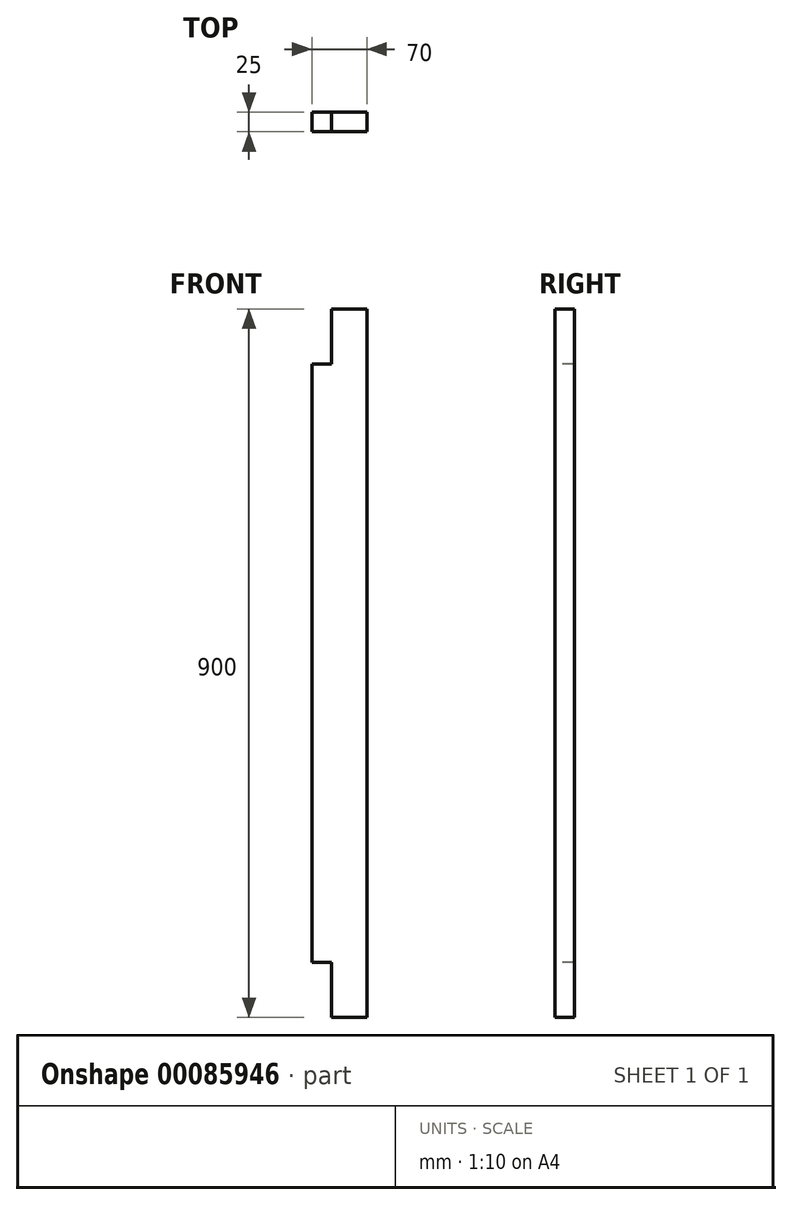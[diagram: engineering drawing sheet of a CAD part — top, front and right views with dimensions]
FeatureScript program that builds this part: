
annotation { "Feature Type Name" : "Feature", "Feature Type Description" : "" }
export const myFeature = defineFeature(function(context is Context, id is Id, definition is map)
    precondition{}
    {
        {
            var Q0;
            Q0=qCreatedBy(makeId("Front.planeOp"),FACE);
            var sketch = newSketch(context, id + "F0", { "sketchPlane" : qUnion([Q0])});
            skLineSegment(sketch, "E0.bottom", {"start": v(35, -450) * mm, "end": v(-35, -450) * mm});
            skLineSegment(sketch, "E0.top", {"start": v(35, 450) * mm, "end": v(-35, 450) * mm});
            skLineSegment(sketch, "E0.left", {"start": v(35, -450) * mm, "end": v(35, 450) * mm});
            skLineSegment(sketch, "E0.right", {"start": v(-35, -450) * mm, "end": v(-35, 450) * mm});
            skPoint(sketch, "E0.middle", {"position": v(0, 0) * mm});
            skSolve(sketch);
        }
        {
            var Q0;
            Q0=makeQuery(id+"F0.imprint","IMPRINT",FACE,{"disambiguationData":[TD([[makeQuery(id+"F0.imprint","IMPRINT",EDGE,{"derivedFrom":sQuery(id+"F0.wireOp",EDGE,"E0.bottom")}),-1.0]])]});
            extrude(context, id + "F1", {"entities" : qUnion([Q0]), "depth" : 25 * mm});
        }
        {
            var Q0;
            Q0=makeQuery(id+"F1.opExtrude","CAP_FACE",FACE,{"disambiguationData":[OSD([sQuery(id+"F0.wireOp",EDGE,"E0.bottom"),sQuery(id+"F0.wireOp",EDGE,"E0.top"),sQuery(id+"F0.wireOp",EDGE,"E0.left"),sQuery(id+"F0.wireOp",EDGE,"E0.right")])],"isStart":false});
            var sketch = newSketch(context, id + "F2", { "sketchPlane" : qUnion([Q0])});
            skLineSegment(sketch, "E1.bottom", {"start": v(-35, 450) * mm, "end": v(-10, 450) * mm});
            skLineSegment(sketch, "E1.top", {"start": v(-35, 380) * mm, "end": v(-10, 380) * mm});
            skLineSegment(sketch, "E1.left", {"start": v(-35, 450) * mm, "end": v(-35, 380) * mm});
            skLineSegment(sketch, "E1.right", {"start": v(-10, 450) * mm, "end": v(-10, 380) * mm});
            skSolve(sketch);
        }
        {
            var Q0;
            Q0=makeQuery(id+"F2.imprint","IMPRINT",FACE,{"disambiguationData":[TD([[makeQuery(id+"F2.imprint","IMPRINT",EDGE,{"derivedFrom":sQuery(id+"F2.wireOp",EDGE,"E1.bottom")}),1.0]])]});
            extrude(context, id + "F3", {"entities" : qUnion([Q0]), "operationType" : NewBodyOperationType.REMOVE, "oppositeDirection" : true, "depth" : 25 * mm});
        }
        {
            var Q0;
            Q0=makeQuery(id+"F1.opExtrude","CAP_FACE",FACE,{"disambiguationData":[OSD([sQuery(id+"F0.wireOp",EDGE,"E0.bottom"),sQuery(id+"F0.wireOp",EDGE,"E0.top"),sQuery(id+"F0.wireOp",EDGE,"E0.left"),sQuery(id+"F0.wireOp",EDGE,"E0.right")])],"isStart":false});
            var sketch = newSketch(context, id + "F4", { "sketchPlane" : qUnion([Q0])});
            skLineSegment(sketch, "E2.bottom", {"start": v(-35, -450) * mm, "end": v(-10, -450) * mm});
            skLineSegment(sketch, "E2.top", {"start": v(-35, -380) * mm, "end": v(-10, -380) * mm});
            skLineSegment(sketch, "E2.left", {"start": v(-35, -450) * mm, "end": v(-35, -380) * mm});
            skLineSegment(sketch, "E2.right", {"start": v(-10, -450) * mm, "end": v(-10, -380) * mm});
            skSolve(sketch);
        }
        {
            var Q0;
            Q0=makeQuery(id+"F4.imprint","IMPRINT",FACE,{"disambiguationData":[TD([[makeQuery(id+"F4.imprint","IMPRINT",EDGE,{"derivedFrom":sQuery(id+"F4.wireOp",EDGE,"E2.bottom")}),-1.0]])]});
            extrude(context, id + "F5", {"entities" : qUnion([Q0]), "operationType" : NewBodyOperationType.REMOVE, "oppositeDirection" : true, "depth" : 25 * mm});
        }
    });
